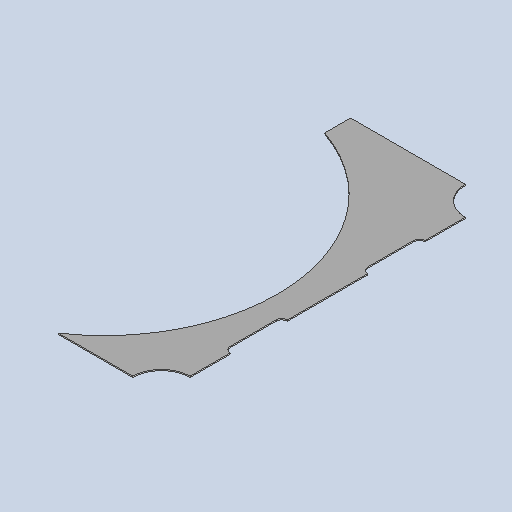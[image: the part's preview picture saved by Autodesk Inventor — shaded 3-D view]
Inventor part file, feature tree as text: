
AUTODESK INVENTOR PART (.ipt)
format: ipt  version: 2025 (Build 290162010, 162A)  size: 276,480 bytes
history: native  units: mm
features: other x4, sketch x2, sheet_metal_op x1
ambient origin geometry x8: Origin, YZ Plane, XZ Plane, XY Plane, X Axis, Y Axis, Z Axis, Center Point
bodies: Solid1 (feature_tree)
feature tree (7):
  sheet_metal_op  "Face1"
  other  "Mark1"
  other  "A-Side Definition"
  sketch  "Sketch1"  dims[d2=2.0mm]
  other  "Plate1"
  sketch  "Sketch2"  dims[d6=200.0mm d9=20.0mm d10=20.0mm d11=20.0mm d22=580.0mm d23=250.0mm d24=302.0mm d25=45.0mm d26=180.0mm d28=100.0mm d29=20.0mm d30=80.0mm d31=170.0mm d32=170.0mm]
  other  "Definition1"
